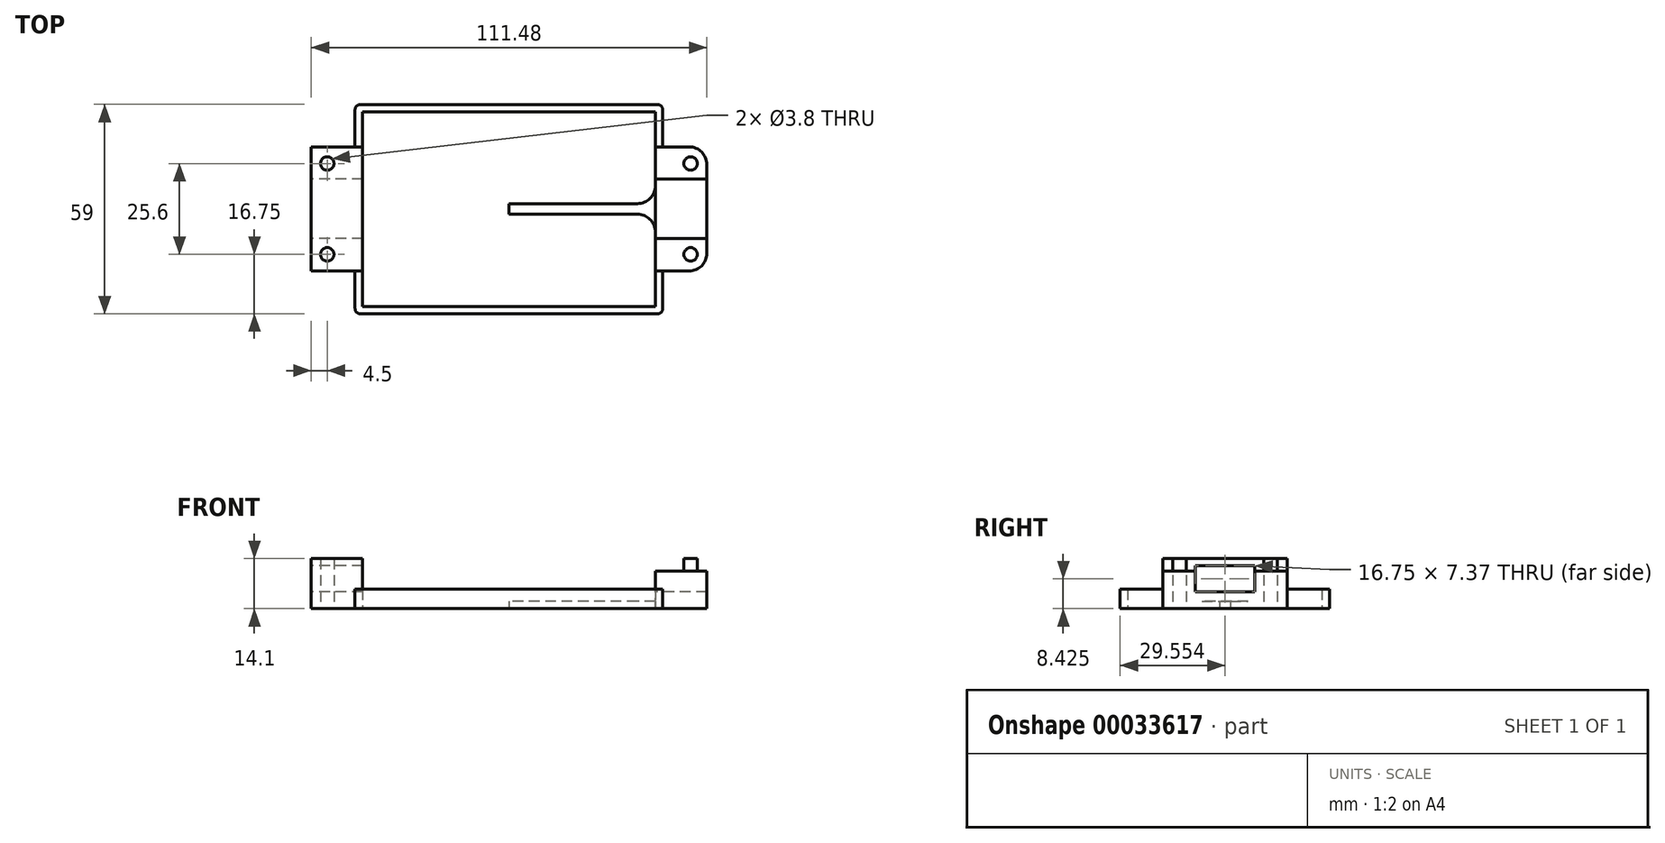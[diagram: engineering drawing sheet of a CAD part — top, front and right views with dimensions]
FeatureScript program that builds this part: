
annotation { "Feature Type Name" : "Feature", "Feature Type Description" : "" }
export const myFeature = defineFeature(function(context is Context, id is Id, definition is map)
    precondition{}
    {
        {
            var Q0;
            Q0=qCreatedBy(makeId("Top.planeOp"),FACE);
            var sketch = newSketch(context, id + "F0", { "sketchPlane" : qUnion([Q0])});
            skCircle(sketch, "E0", {"center": v(0, 0) * mm, "radius": 1.9 * mm});
            skCircle(sketch, "E1", {"center": v(0, -25.6) * mm, "radius": 1.9 * mm});
            skLineSegment(sketch, "E2.rect.bottom", {"start": v(4.5, -30.3) * mm, "end": v(-4.5, -30.3) * mm});
            skLineSegment(sketch, "E2.rect.top", {"start": v(4.5, 4.7) * mm, "end": v(-4.5, 4.7) * mm});
            skLineSegment(sketch, "E2.rect.right", {"start": v(-4.5, -30.3) * mm, "end": v(-4.5, 4.7) * mm});
            skPoint(sketch, "E2.rect.middle", {"position": v(0, -12.8) * mm});
            skLineSegment(sketch, "E3", {"start": v(67.3, -11.3) * mm, "end": v(14.95, -11.3) * mm});
            skLineSegment(sketch, "E4", {"start": v(67.3, -14.3) * mm, "end": v(14.95, -14.3) * mm});
            skPoint(sketch, "E5.MirrorP", {"position": v(76.8, -12.8) * mm});
            skLineSegment(sketch, "E6.MirrorCS", {"start": v(9.5, -14.3) * mm, "end": v(9.95, -14.3) * mm});
            skPoint(sketch, "E7.start.orphan", {"position": v(4.5, 0) * mm});
            skPoint(sketch, "E8.orphan", {"position": v(25.6, 0) * mm});
            skPoint(sketch, "E9.start.orphan", {"position": v(38.4, 0) * mm});
            skPoint(sketch, "E10.orphan", {"position": v(51.2, 0) * mm});
            skPoint(sketch, "E11.visualSharp", {"position": v(72.3, -11.3) * mm});
            skPoint(sketch, "E12.visualSharp", {"position": v(4.5, -11.3) * mm});
            skPoint(sketch, "E13.visualSharp", {"position": v(4.5, -14.3) * mm});
            skCircle(sketch, "E14", {"center": v(102.4, -25.6) * mm, "radius": 1.9 * mm});
            skLineSegment(sketch, "E15.rect.bottom", {"start": v(106.98, -30.3) * mm, "end": v(97.82, -30.3) * mm});
            skLineSegment(sketch, "E15.rect.top", {"start": v(106.98, 4.7) * mm, "end": v(97.82, 4.7) * mm});
            skLineSegment(sketch, "E15.rect.left", {"start": v(106.98, -30.3) * mm, "end": v(106.98, 4.7) * mm});
            skPoint(sketch, "E15.rect.middle", {"position": v(102.4, -12.8) * mm});
            skLineSegment(sketch, "E16", {"start": v(72.3, -11.3) * mm, "end": v(87.45, -11.3) * mm});
            skLineSegment(sketch, "E17", {"start": v(72.3, -14.3) * mm, "end": v(87.45, -14.3) * mm});
            skLineSegment(sketch, "E18", {"start": v(51.2, -25.6) * mm, "end": v(51.2, 0) * mm});
            skLineSegment(sketch, "E19", {"start": v(97.82, -30.3) * mm, "end": v(92.45, -30.3) * mm});
            skLineSegment(sketch, "E20", {"start": v(92.45, -30.3) * mm, "end": v(92.45, -19.3) * mm});
            skLineSegment(sketch, "E21", {"start": v(92.45, 4.7) * mm, "end": v(97.82, 4.7) * mm});
            skLineSegment(sketch, "E22.trimOffspring", {"start": v(92.45, -6.3) * mm, "end": v(92.45, 4.7) * mm});
            skPoint(sketch, "E23.visualSharp", {"position": v(92.45, -11.3) * mm});
            skArc(sketch, "E23.filletArc", {"start": v(87.45, -11.3) * mm, "mid": v(90.99, -9.84) * mm, "end": v(92.45, -6.3) * mm});
            skPoint(sketch, "E24.visualSharp", {"position": v(92.45, -14.3) * mm});
            skArc(sketch, "E24.filletArc", {"start": v(92.45, -19.3) * mm, "mid": v(90.99, -15.76) * mm, "end": v(87.45, -14.3) * mm});
            skArc(sketch, "E25.MirrorCS", {"start": v(14.95, -11.3) * mm, "mid": v(11.41, -9.84) * mm, "end": v(9.95, -6.3) * mm});
            skPoint(sketch, "E26.MirrorP", {"position": v(25.6, -12.8) * mm});
            skArc(sketch, "E27.MirrorCS", {"start": v(9.95, -19.3) * mm, "mid": v(11.41, -15.76) * mm, "end": v(14.95, -14.3) * mm});
            skLineSegment(sketch, "E28.MirrorCS", {"start": v(9.95, 4.7) * mm, "end": v(4.58, 4.7) * mm});
            skLineSegment(sketch, "E29.MirrorCS", {"start": v(4.58, -30.3) * mm, "end": v(9.95, -30.3) * mm});
            skLineSegment(sketch, "E30.MirrorCS", {"start": v(-4.58, 4.7) * mm, "end": v(4.58, 4.7) * mm});
            skPoint(sketch, "E31.MirrorP", {"position": v(9.95, -14.3) * mm});
            skLineSegment(sketch, "E32.MirrorCS", {"start": v(-4.58, -30.3) * mm, "end": v(4.58, -30.3) * mm});
            skLineSegment(sketch, "E33.MirrorCS", {"start": v(-4.58, -30.3) * mm, "end": v(-4.58, 4.7) * mm});
            skLineSegment(sketch, "E34.MirrorCS", {"start": v(9.95, -6.3) * mm, "end": v(9.95, 4.7) * mm});
            skLineSegment(sketch, "E35.MirrorCS", {"start": v(9.95, -30.3) * mm, "end": v(9.95, -19.3) * mm});
            skPoint(sketch, "E36.MirrorP", {"position": v(9.95, -11.3) * mm});
            skLineSegment(sketch, "E37.trimOffspring", {"start": v(14.95, -14.3) * mm, "end": v(72.3, -14.3) * mm});
            skLineSegment(sketch, "E38.trimOffspring", {"start": v(9.95, -11.3) * mm, "end": v(9.5, -11.3) * mm});
            skLineSegment(sketch, "E39.trimOffspring", {"start": v(9.95, -14.3) * mm, "end": v(9.5, -14.3) * mm});
            skLineSegment(sketch, "E40", {"start": v(67.3, -11.3) * mm, "end": v(72.3, -11.3) * mm});
            skLineSegment(sketch, "E41", {"start": v(102.4, -25.6) * mm, "end": v(102.4, 0) * mm});
            skCircle(sketch, "E42", {"center": v(102.4, 0) * mm, "radius": 1.9 * mm});
            skLineSegment(sketch, "E43", {"start": v(9.95, -6.3) * mm, "end": v(9.95, -19.3) * mm});
            skLineSegment(sketch, "E44", {"start": v(92.45, -6.3) * mm, "end": v(92.45, -19.3) * mm});
            skSolve(sketch);
        }
        {
            var Q0;
            Q0=makeQuery(id+"F0.imprint","IMPRINT",FACE,{"disambiguationData":[TD([[makeQuery(id+"F0.imprint","IMPRINT",EDGE,{"derivedFrom":sQuery(id+"F0.wireOp",EDGE,"E42")}),1.0]])]});
            var Q1;
            Q1=makeQuery(id+"F0.imprint","IMPRINT",FACE,{"disambiguationData":[TD([[makeQuery(id+"F0.imprint","IMPRINT",EDGE,{"derivedFrom":sQuery(id+"F0.wireOp",EDGE,"E14")}),1.0]])]});
            var Q2;
            Q2=makeQuery(id+"F0.imprint","IMPRINT",FACE,{"disambiguationData":[TD([[makeQuery(id+"F0.imprint","IMPRINT",EDGE,{"derivedFrom":sQuery(id+"F0.wireOp",EDGE,"E1")}),-1.0]])]});
            var Q3;
            Q3=makeQuery(id+"F0.imprint","IMPRINT",FACE,{"disambiguationData":[TD([[makeQuery(id+"F0.imprint","IMPRINT",EDGE,{"derivedFrom":sQuery(id+"F0.wireOp",EDGE,"E0")}),-1.0]])]});
            extrude(context, id + "F1", {"entities" : qUnion([Q0, Q1, Q2, Q3]), "depth" : (8.5 + 2.1 + 3.5) * mm});
        }
        {
            var Q0;
            {var subQ4=sQuery(id+"F0.wireOp",EDGE,"E25.MirrorCS");Q0=makeQuery(id+"F0.imprint","IMPRINT",FACE,{"disambiguationData":[TD([[makeQuery(id+"F0.imprint","IMPRINT",EDGE,{"derivedFrom":subQ4}),1.0]])]});}
            var Q1;
            Q1=makeQuery(id+"F0.imprint","IMPRINT",FACE,{"disambiguationData":[TD([[makeQuery(id+"F0.imprint","IMPRINT",EDGE,{"derivedFrom":sQuery(id+"F0.wireOp",EDGE,"E16")}),-1.0]])]});
            extrude(context, id + "F2", {"entities" : qUnion([Q0, Q1]), "operationType" : NewBodyOperationType.ADD, "depth" : 2.1 * mm});
        }
        {
            var Q0;
            {var subQ0=sQuery(id+"F0.wireOp",EDGE,"E2.rect.right");Q0=makeQuery(id+"F0.imprint","IMPRINT",FACE,{"disambiguationData":[TD([[makeQuery(id+"F0.imprint","IMPRINT",EDGE,{"derivedFrom":subQ0}),-1.0]])]});}
            var Q1;
            Q1=makeQuery(id+"F0.imprint","IMPRINT",FACE,{"disambiguationData":[TD([[makeQuery(id+"F0.imprint","IMPRINT",EDGE,{"derivedFrom":sQuery(id+"F0.wireOp",EDGE,"E14")}),-1.0]])]});
            extrude(context, id + "F3", {"entities" : qUnion([Q0, Q1]), "operationType" : NewBodyOperationType.ADD, "depth" : (8.5 + 2.1) * mm});
        }
        {
            var Q0;
            Q0=qCreatedBy(makeId("Right.planeOp"),FACE);
            var sketch = newSketch(context, id + "F4", { "sketchPlane" : qUnion([Q0])});
            skLineSegment(sketch, "E45", {"start": v(-4.42, 12.11) * mm, "end": v(-21.17, 12.11) * mm});
            skLineSegment(sketch, "E46.rect.top", {"start": v(-21.17, 4.74) * mm, "end": v(-4.42, 4.74) * mm});
            skLineSegment(sketch, "E46.rect.left", {"start": v(-21.17, 12.11) * mm, "end": v(-21.17, 4.74) * mm});
            skLineSegment(sketch, "E46.rect.right", {"start": v(-4.42, 12.11) * mm, "end": v(-4.42, 4.74) * mm});
            skPoint(sketch, "E46.rect.middle", {"position": v(-12.8, 12.11) * mm});
            skPoint(sketch, "E47.orphan", {"position": v(4.7, 12.11) * mm});
            skPoint(sketch, "E46.rect.bottom.end.orphan", {"position": v(-4.42, 19.49) * mm});
            skPoint(sketch, "E48.orphan", {"position": v(-21.17, 19.49) * mm});
            skPoint(sketch, "E49.orphan", {"position": v(-30.3, 12.11) * mm});
            skSolve(sketch);
        }
        {
            var Q0;
            Q0=makeQuery(id+"F4.imprint","IMPRINT",FACE,{"disambiguationData":[TD([[makeQuery(id+"F4.imprint","IMPRINT",EDGE,{"derivedFrom":sQuery(id+"F4.wireOp",EDGE,"E45")}),1.0]])]});
            extrude(context, id + "F5", {"entities" : qUnion([Q0]), "operationType" : NewBodyOperationType.REMOVE, "endBound" : BoundingType.SYMMETRIC, "depth" : 300 * mm});
        }
        {
            var Q0;
            Q0=makeQuery(id+"F3.opExtrude","SWEPT_EDGE",EDGE,{"disambiguationData":[OSD([sQuery(id+"F0.wireOp",EDGE,"E2.rect.right"),sQuery(id+"F0.wireOp",EDGE,"E30.MirrorCS")])]});
            var Q1;
            Q1=makeQuery(id+"F3.opExtrude","SWEPT_EDGE",EDGE,{"disambiguationData":[OSD([sQuery(id+"F0.wireOp",EDGE,"E2.rect.right"),sQuery(id+"F0.wireOp",EDGE,"E32.MirrorCS")])]});
            var Q2;
            Q2=makeQuery(id+"F3.opExtrude","SWEPT_EDGE",EDGE,{"disambiguationData":[OSD([sQuery(id+"F0.wireOp",EDGE,"E15.rect.top"),sQuery(id+"F0.wireOp",EDGE,"E15.rect.left")])]});
            var Q3;
            Q3=makeQuery(id+"F3.opExtrude","SWEPT_EDGE",EDGE,{"disambiguationData":[OSD([sQuery(id+"F0.wireOp",EDGE,"E15.rect.bottom"),sQuery(id+"F0.wireOp",EDGE,"E15.rect.left")])]});
            fillet(context, id + "F6", {"entities" : qUnion([Q0, Q1, Q2, Q3]), "radius" : 5 * mm, "tangentPropagation" : true, "allowEdgeOverflow" : false});
        }
        {
            var Q0;
            Q0=qCreatedBy(makeId("Top.planeOp"),FACE);
            var sketch = newSketch(context, id + "F7", { "sketchPlane" : qUnion([Q0])});
            skLineSegment(sketch, "E50", {"start": v(0, 0) * mm, "end": v(9.93, 0) * mm});
            skLineSegment(sketch, "E51", {"start": v(9.93, 4.74) * mm, "end": v(9.93, 14.55) * mm});
            skLineSegment(sketch, "E52", {"start": v(9.93, 14.55) * mm, "end": v(12.93, 14.55) * mm});
            skLineSegment(sketch, "E53", {"start": v(12.93, 14.55) * mm, "end": v(12.93, 16.65) * mm});
            skLineSegment(sketch, "E54", {"start": v(12.93, 16.65) * mm, "end": v(7.83, 16.65) * mm});
            skLineSegment(sketch, "E55", {"start": v(7.83, 16.65) * mm, "end": v(7.83, 9.64) * mm});
            skLineSegment(sketch, "E56", {"start": v(7.83, 9.64) * mm, "end": v(7.83, 4.74) * mm});
            skLineSegment(sketch, "E57", {"start": v(0, -12.85) * mm, "end": v(6.48, -12.85) * mm});
            skLineSegment(sketch, "E58.MirrorCS", {"start": v(12.93, -40.25) * mm, "end": v(12.93, -42.35) * mm});
            skLineSegment(sketch, "E59.MirrorCS", {"start": v(9.93, -40.25) * mm, "end": v(12.93, -40.25) * mm});
            skLineSegment(sketch, "E60.MirrorCS", {"start": v(9.93, -30.45) * mm, "end": v(9.93, -40.25) * mm});
            skLineSegment(sketch, "E61.MirrorCS", {"start": v(7.83, -42.35) * mm, "end": v(7.83, -35.35) * mm});
            skLineSegment(sketch, "E62.MirrorCS", {"start": v(7.83, -35.35) * mm, "end": v(7.83, -30.45) * mm});
            skLineSegment(sketch, "E63.MirrorCS", {"start": v(12.93, -42.35) * mm, "end": v(7.83, -42.35) * mm});
            skLineSegment(sketch, "E64.MirrorCS", {"start": v(89.47, -40.25) * mm, "end": v(89.47, -42.35) * mm});
            skLineSegment(sketch, "E65.MirrorCS", {"start": v(92.47, -40.25) * mm, "end": v(89.47, -40.25) * mm});
            skLineSegment(sketch, "E66.MirrorCS", {"start": v(89.47, 14.55) * mm, "end": v(89.47, 16.65) * mm});
            skLineSegment(sketch, "E67.MirrorCS", {"start": v(92.47, 14.55) * mm, "end": v(89.47, 14.55) * mm});
            skLineSegment(sketch, "E68.MirrorCS", {"start": v(94.57, 9.64) * mm, "end": v(94.57, 4.74) * mm});
            skLineSegment(sketch, "E69.MirrorCS", {"start": v(89.47, 16.65) * mm, "end": v(94.57, 16.65) * mm});
            skLineSegment(sketch, "E70.MirrorCS", {"start": v(89.47, -42.35) * mm, "end": v(94.57, -42.35) * mm});
            skLineSegment(sketch, "E71.MirrorCS", {"start": v(94.57, -42.35) * mm, "end": v(94.57, -35.35) * mm});
            skLineSegment(sketch, "E72.MirrorCS", {"start": v(92.47, -30.45) * mm, "end": v(92.47, -40.25) * mm});
            skLineSegment(sketch, "E73.MirrorCS", {"start": v(92.47, 4.74) * mm, "end": v(92.47, 14.55) * mm});
            skLineSegment(sketch, "E74.MirrorCS", {"start": v(94.57, 16.65) * mm, "end": v(94.57, 9.64) * mm});
            skLineSegment(sketch, "E75.MirrorCS", {"start": v(94.57, -35.35) * mm, "end": v(94.57, -30.45) * mm});
            skPoint(sketch, "E76.MirrorCS.start.orphan", {"position": v(92.47, 9.64) * mm});
            skPoint(sketch, "E77.MirrorCS.start.orphan", {"position": v(92.47, 0) * mm});
            skLineSegment(sketch, "E78", {"start": v(9.93, 4.74) * mm, "end": v(9.93, 4.13) * mm});
            skLineSegment(sketch, "E79", {"start": v(9.93, 4.13) * mm, "end": v(7.83, 4.13) * mm});
            skLineSegment(sketch, "E80", {"start": v(7.83, 4.13) * mm, "end": v(7.83, 4.74) * mm});
            skLineSegment(sketch, "E81", {"start": v(94.57, 4.74) * mm, "end": v(94.57, 4.38) * mm});
            skLineSegment(sketch, "E82", {"start": v(94.57, 4.38) * mm, "end": v(92.47, 4.38) * mm});
            skLineSegment(sketch, "E83", {"start": v(92.47, 4.38) * mm, "end": v(92.47, 4.74) * mm});
            skLineSegment(sketch, "E84", {"start": v(94.57, -30.45) * mm, "end": v(94.57, -29.96) * mm});
            skLineSegment(sketch, "E85", {"start": v(94.57, -29.96) * mm, "end": v(92.47, -29.96) * mm});
            skLineSegment(sketch, "E86", {"start": v(92.47, -29.96) * mm, "end": v(92.47, -30.45) * mm});
            skLineSegment(sketch, "E87", {"start": v(9.93, -30.45) * mm, "end": v(9.93, -29.83) * mm});
            skLineSegment(sketch, "E88", {"start": v(9.93, -29.83) * mm, "end": v(7.83, -29.83) * mm});
            skLineSegment(sketch, "E89", {"start": v(7.83, -29.83) * mm, "end": v(7.83, -30.45) * mm});
            skLineSegment(sketch, "E90", {"start": v(12.93, 16.65) * mm, "end": v(89.47, 16.65) * mm});
            skLineSegment(sketch, "E91", {"start": v(12.93, 14.55) * mm, "end": v(89.47, 14.55) * mm});
            skLineSegment(sketch, "E92", {"start": v(12.93, -40.25) * mm, "end": v(89.47, -40.25) * mm});
            skLineSegment(sketch, "E93", {"start": v(12.93, -42.35) * mm, "end": v(89.47, -42.35) * mm});
            skSolve(sketch);
        }
        {
            var Q0;
            Q0 = qSketchRegion(id + "F7", true);
            extrude(context, id + "F8", {"entities" : qUnion([Q0]), "operationType" : NewBodyOperationType.ADD, "depth" : 5.5 * mm});
        }
        {
            var Q0;
            Q0=makeQuery(id+"F8.opExtrude","SWEPT_EDGE",EDGE,{"disambiguationData":[OSD([sQuery(id+"F7.wireOp",EDGE,"E70.MirrorCS"),sQuery(id+"F7.wireOp",EDGE,"E71.MirrorCS")])]});
            var Q1;
            Q1=makeQuery(id+"F8.opExtrude","SWEPT_EDGE",EDGE,{"disambiguationData":[OSD([sQuery(id+"F7.wireOp",EDGE,"E69.MirrorCS"),sQuery(id+"F7.wireOp",EDGE,"E74.MirrorCS")])]});
            var Q2;
            Q2=makeQuery(id+"F8.opExtrude","SWEPT_EDGE",EDGE,{"disambiguationData":[OSD([sQuery(id+"F7.wireOp",EDGE,"E54"),sQuery(id+"F7.wireOp",EDGE,"E55")])]});
            var Q3;
            Q3=makeQuery(id+"F8.opExtrude","SWEPT_EDGE",EDGE,{"disambiguationData":[OSD([sQuery(id+"F7.wireOp",EDGE,"E63.MirrorCS"),sQuery(id+"F7.wireOp",EDGE,"E61.MirrorCS")])]});
            fillet(context, id + "F9", {"entities" : qUnion([Q0, Q1, Q2, Q3]), "radius" : 1.5 * mm, "tangentPropagation" : true, "allowEdgeOverflow" : false});
        }
    });
